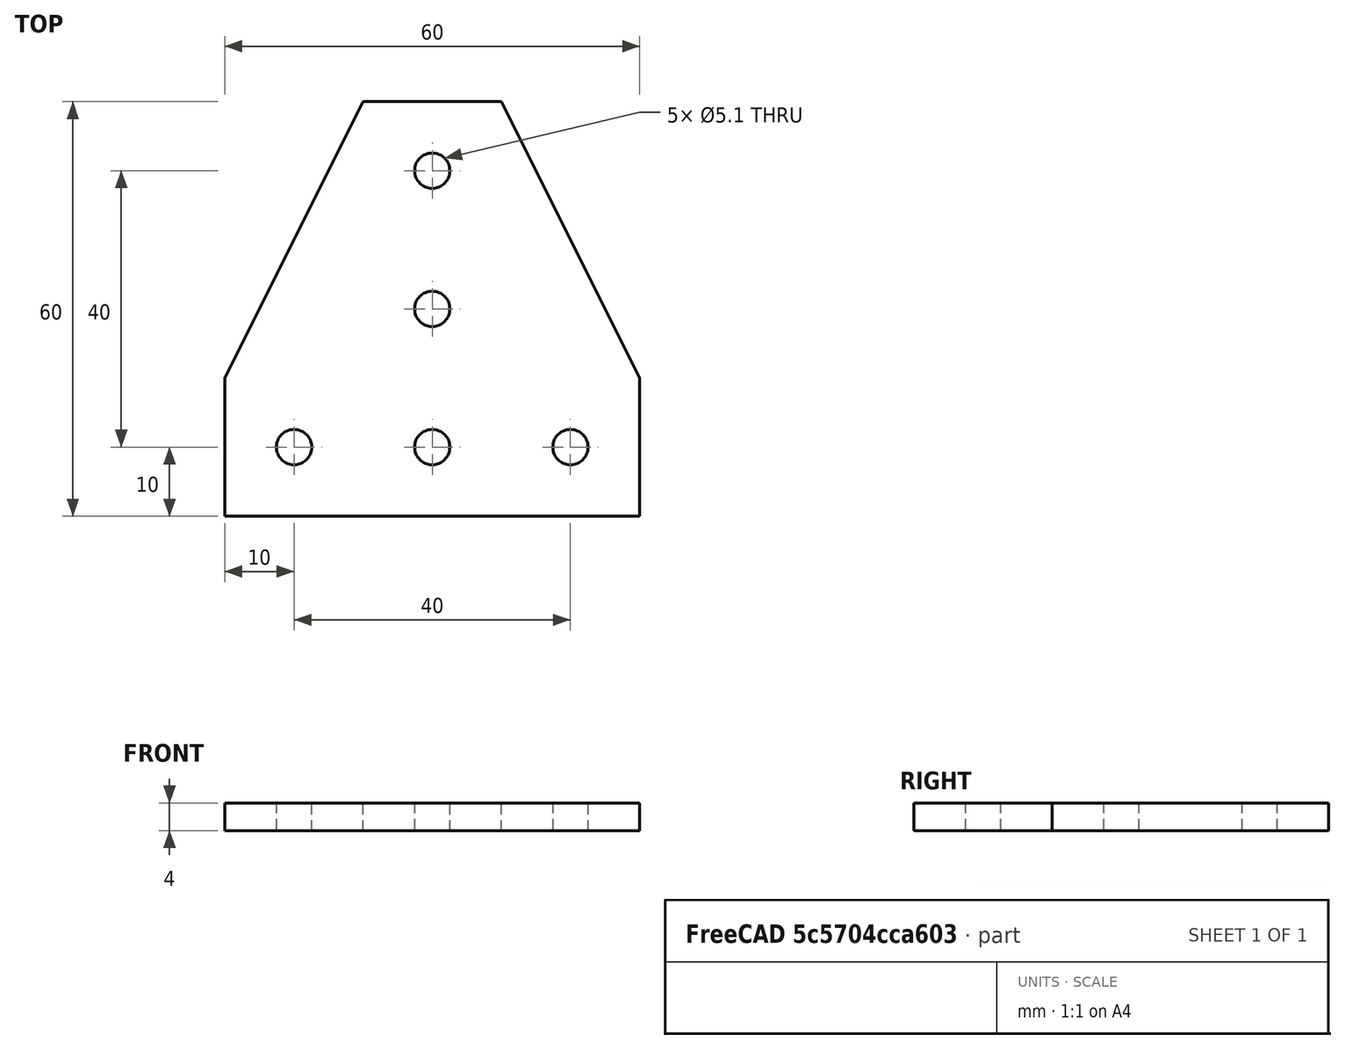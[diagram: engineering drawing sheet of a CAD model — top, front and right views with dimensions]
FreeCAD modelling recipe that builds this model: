
FCSTD DOCUMENT  (FreeCAD 0.20R25645 (Git))
Label: 2020 T plate
License: All rights reserved
LicenseURL: http://en.wikipedia.org/wiki/All_rights_reserved
objects: Sketcher::SketchObject×1, PartDesign::Pad×1, PartDesign::Body×1
note: 4 computed .brp shape members not serialized (recipe doc carries the construction recipe); baked Part::Feature solids carry a one-line shape summary decoded from their .brp

FEATURE [Sketcher::SketchObject] Sketch
  FullyConstrained = true
  MapMode = 5
  Support = -> [XY_Plane]
  sketch-geometry (18):
    g0: LineSegment StartX=0 StartY=0 StartZ=0 EndX=60 EndY=0 EndZ=0
    g1: LineSegment StartX=0 StartY=0 StartZ=0 EndX=0 EndY=20 EndZ=0
    g2: LineSegment StartX=0 StartY=20 StartZ=0 EndX=20 EndY=60 EndZ=0
    g3: LineSegment StartX=20 StartY=60 StartZ=0 EndX=40 EndY=60 EndZ=0
    g4: LineSegment StartX=40 StartY=60 StartZ=0 EndX=60 EndY=20 EndZ=0
    g5: LineSegment StartX=60 StartY=20 StartZ=0 EndX=60 EndY=0 EndZ=0
    g6: LineSegment StartX=20 StartY=60 StartZ=0 EndX=20 EndY=0 EndZ=0
    g7: Circle CenterX=30 CenterY=10 CenterZ=0 NormalX=0 NormalY=0 NormalZ=1 AngleXU=0 Radius=2.55
    g8: LineSegment StartX=30 StartY=10 StartZ=0 EndX=30 EndY=30 EndZ=0
    g9: LineSegment StartX=30 StartY=30 StartZ=0 EndX=30 EndY=50 EndZ=0
    g10: LineSegment StartX=30 StartY=10 StartZ=0 EndX=30 EndY=0 EndZ=0
    g11: LineSegment StartX=30 StartY=10 StartZ=0 EndX=20 EndY=10 EndZ=0
    g12: LineSegment StartX=30 StartY=10 StartZ=0 EndX=50 EndY=10 EndZ=0
    g13: LineSegment StartX=30 StartY=10 StartZ=0 EndX=10 EndY=10 EndZ=0
    g14: Circle CenterX=10 CenterY=10 CenterZ=0 NormalX=0 NormalY=0 NormalZ=1 AngleXU=0 Radius=2.55
    g15: Circle CenterX=50 CenterY=10 CenterZ=0 NormalX=0 NormalY=0 NormalZ=1 AngleXU=0 Radius=2.55
    g16: Circle CenterX=30 CenterY=30 CenterZ=0 NormalX=0 NormalY=0 NormalZ=1 AngleXU=0 Radius=2.55
    g17: Circle CenterX=30 CenterY=50 CenterZ=0 NormalX=0 NormalY=0 NormalZ=1 AngleXU=0 Radius=2.55
  constraints (49):
    c: Coincident(g0,g-1)
    c: PointOnObject(g0,g-1)
    c: DistanceX(g0,g0) = 60
    c: Coincident(g1,g0)
    c: PointOnObject(g1,g-2)
    c: DistanceY(g1,g1) = 20
    c: Coincident(g2,g1)
    c: Coincident(g3,g2)
    c: Horizontal(g3)
    c: Coincident(g4,g3)
    c: Coincident(g5,g4)
    c: Coincident(g5,g0)
    c: Equal(g1,g3)
    c: Equal(g1,g5)
    c: Equal(g2,g4)
    c: Vertical(g5)
    c: Coincident(g6,g2)
    c: PointOnObject(g6,g0)
    c: Vertical(g6)
    c: Equal(g0,g6)
    c: Diameter(g7) = 5.1
    c: Coincident(g8,g7)
    c: Vertical(g8)
    c: Coincident(g9,g8)
    c: Vertical(g9)
    c: Coincident(g10,g7)
    c: PointOnObject(g10,g0)
    c: Vertical(g10)
    c: Coincident(g11,g7)
    c: PointOnObject(g11,g6)
    c: Horizontal(g11)
    c: DistanceX(g11,g11) = 10
    c: Equal(g11,g10)
    c: Coincident(g12,g7)
    c: Horizontal(g12)
    c: Coincident(g13,g7)
    c: Horizontal(g13)
    c: DistanceX(g13,g13) = 20
    c: Equal(g13,g12)
    c: Equal(g13,g8)
    c: Equal(g13,g9)
    c: Coincident(g14,g13)
    c: Coincident(g15,g12)
    c: Equal(g7,g14)
    c: Equal(g7,g15)
    c: Coincident(g16,g8)
    c: Coincident(g17,g9)
    c: Equal(g7,g16)
    c: Equal(g7,g17)
FEATURE [PartDesign::Pad] Pad
  Direction = (0,0,1)
  Length = 4
  Length2 = 100
  Profile = -> Sketch
  Type = 0
FEATURE [PartDesign::Body] Body
  Group = -> [Sketch,Pad]
  Origin = -> Origin
  Tip = -> Pad
